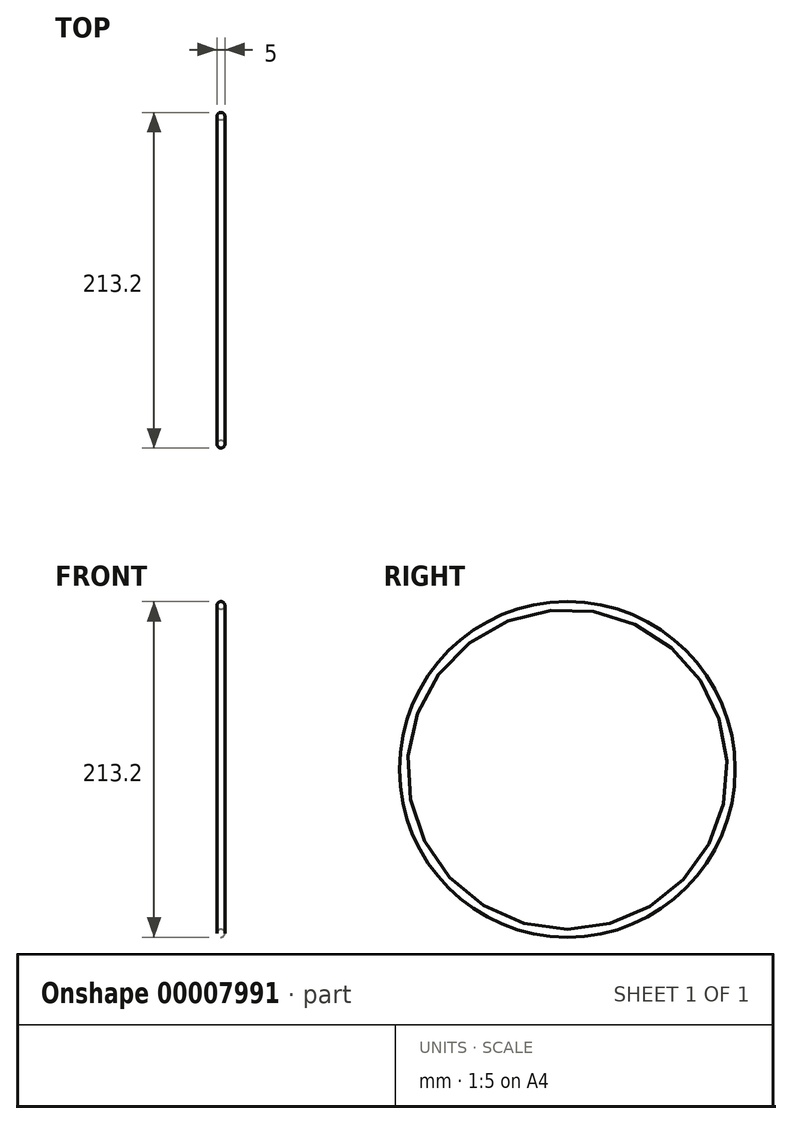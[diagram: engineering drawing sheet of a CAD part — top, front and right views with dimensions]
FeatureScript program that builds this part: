
annotation { "Feature Type Name" : "Feature", "Feature Type Description" : "" }
export const myFeature = defineFeature(function(context is Context, id is Id, definition is map)
    precondition{}
    {
        {
            var Q0;
            Q0=qCreatedBy(makeId("Front.planeOp"),FACE);
            var sketch = newSketch(context, id + "F0", { "sketchPlane" : qUnion([Q0])});
            skLineSegment(sketch, "E0", {"start": v(0, 0) * mm, "end": v(-236.85, 0) * mm, "construction": true});
            skLineSegment(sketch, "E1", {"start": v(-0.07, 101.6) * mm, "end": v(-0.07, 77.2) * mm});
            skLineSegment(sketch, "E2", {"start": v(-0.07, 77.2) * mm, "end": v(35.48, 77.2) * mm});
            skLineSegment(sketch, "E3", {"start": v(35.48, 77.2) * mm, "end": v(35.48, 65.2) * mm});
            skLineSegment(sketch, "E4", {"start": v(35.48, 65.2) * mm, "end": v(119.93, 65.2) * mm});
            skLineSegment(sketch, "E5", {"start": v(119.93, 65.2) * mm, "end": v(119.93, 76.2) * mm});
            skLineSegment(sketch, "E6", {"start": v(119.93, 76.2) * mm, "end": v(46.48, 76.2) * mm});
            skLineSegment(sketch, "E7", {"start": v(46.48, 76.2) * mm, "end": v(46.48, 88.2) * mm});
            skLineSegment(sketch, "E8", {"start": v(46.48, 88.2) * mm, "end": v(14.93, 88.2) * mm});
            skLineSegment(sketch, "E9", {"start": v(14.93, 88.2) * mm, "end": v(14.93, 101.6) * mm});
            skLineSegment(sketch, "E10", {"start": v(-0.07, 101.6) * mm, "end": v(14.93, 101.6) * mm});
            skLineSegment(sketch, "E11", {"start": v(2.94, 101.6) * mm, "end": v(2.94, 139.5) * mm});
            skLineSegment(sketch, "E12", {"start": v(2.94, 139.5) * mm, "end": v(35.48, 139.5) * mm});
            skLineSegment(sketch, "E13", {"start": v(35.48, 139.5) * mm, "end": v(35.48, 88.2) * mm});
            skLineSegment(sketch, "E14", {"start": v(35.48, 88.2) * mm, "end": v(14.93, 88.2) * mm});
            skLineSegment(sketch, "E15", {"start": v(14.93, 101.6) * mm, "end": v(2.94, 101.6) * mm});
            skCircle(sketch, "E16", {"center": v(0.44, 104.1) * mm, "radius": 2.5 * mm});
            skSolve(sketch);
        }
        {
            var Q0;
            {var subQ0=sQuery(id+"F0.wireOp",EDGE,"E16");var subQ2=makeQuery(id+"F0.imprint","INTERSECT",VERTEX,{"derivedFrom":[sQuery(id+"F0.wireOp",EDGE,"E10"),subQ0]});Q0=makeQuery(id+"F0.imprint","IMPRINT",FACE,{"disambiguationData":[TD([[makeQuery(id+"F0.imprint","IMPRINT",EDGE,{"disambiguationData":[TD([[subQ2,1.0]])],"derivedFrom":subQ0}),1.0]])]});}
            var Q1;
            Q1=sQuery(id+"F0.wireOp",EDGE,"E0");
            revolve(context, id + "F1", {"entities" : qUnion([Q0]), "axis" : qUnion([Q1]), "revolveType" : RevolveType.FULL});
        }
    });
